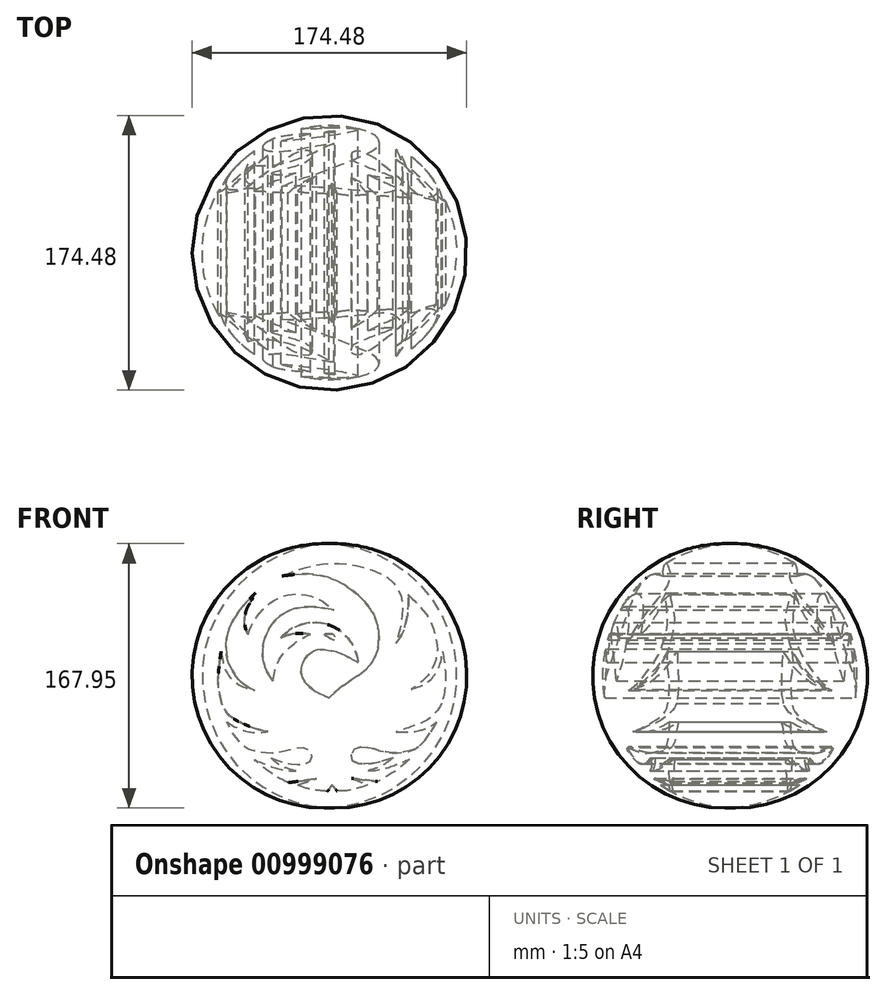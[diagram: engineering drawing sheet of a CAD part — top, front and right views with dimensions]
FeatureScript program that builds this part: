
annotation { "Feature Type Name" : "Feature", "Feature Type Description" : "" }
export const myFeature = defineFeature(function(context is Context, id is Id, definition is map)
    precondition{}
    {
        {
            var Q0;
            Q0=qCreatedBy(makeId("Front.planeOp"),FACE);
            var sketch = newSketch(context, id + "F0", { "sketchPlane" : qUnion([Q0])});
            skArc(sketch, "E0", {"start": v(18.3, 8.55) * mm, "mid": v(-1.06, 32.74) * mm, "end": v(-30.86, 24.24) * mm});
            skArc(sketch, "E1", {"start": v(-11.86, 26.45) * mm, "mid": v(-21.55, 26.98) * mm, "end": v(-30.86, 24.24) * mm});
            skFitSpline(sketch, "E2", {"points": [v(18.3, 8.55) * mm, v(12.24, 11.99) * mm, v(4.4, 15.3) * mm, v(-2.22, 16.67) * mm, v(-7.17, 16.67) * mm, v(-12.96, 14.05) * mm, v(-16.95, 8.55) * mm, v(-17.92, 2.49) * mm, v(-16.13, -3.02) * mm, v(-11.44, -7.84) * mm, v(-6.07, -11.15) * mm, v(-0.36, -13.9) * mm], "startDerivative": vector(-61.39, 36.74) * mm, "endDerivative": vector(64.34, -29.86) * mm});
            skFitSpline(sketch, "E3", {"points": [v(-11.86, 26.45) * mm, v(-18.58, 23.24) * mm, v(-27.67, 15.96) * mm, v(-32.05, 10.02) * mm, v(-34.76, 2.93) * mm, v(-35.8, -3) * mm], "startDerivative": vector(-33.06, -13.18) * mm, "endDerivative": vector(-4.26, -33.04) * mm});
            skFitSpline(sketch, "E4", {"points": [v(-35.8, -3) * mm, v(-40.57, 4.73) * mm, v(-42.38, 16.67) * mm, v(-38.38, 30.03) * mm, v(-27.54, 40.74) * mm, v(-11.86, 44.1) * mm, v(2.79, 42.03) * mm], "startDerivative": vector(-38.89, 52.02) * mm, "endDerivative": vector(81.86, -17.1) * mm});
            skFitSpline(sketch, "E5", {"points": [v(2.79, 42.03) * mm, v(-7.17, 49) * mm, v(-19.02, 52.1) * mm, v(-29.47, 50.67) * mm, v(-40.05, 44.48) * mm, v(-48.7, 33.38) * mm, v(-51.67, 26.45) * mm], "startDerivative": vector(-54.73, 44.88) * mm, "endDerivative": vector(-17.06, -47.9) * mm});
            skFitSpline(sketch, "E6", {"points": [v(-51.67, 26.45) * mm, v(-53.73, 32.48) * mm, v(-52.7, 42.03) * mm, v(-49.22, 48.6) * mm, v(-46.9, 52.87) * mm], "startDerivative": vector(-10.86, 23.04) * mm, "endDerivative": vector(10.17, 19.75) * mm});
            skFitSpline(sketch, "E7", {"points": [v(-46.9, 52.87) * mm, v(-54.25, 45.12) * mm, v(-61.86, 34.15) * mm, v(-65.22, 23.96) * mm, v(-65.22, 12.86) * mm, v(-61.86, 3.96) * mm, v(-55.67, -4.04) * mm, v(-47.6, -9.08) * mm], "startDerivative": vector(-51.07, -50.55) * mm, "endDerivative": vector(62.87, -32.4) * mm});
            skFitSpline(sketch, "E8", {"points": [v(-47.6, -9.08) * mm, v(-59.02, -4.56) * mm, v(-66.12, 4.35) * mm, v(-68.83, 15.57) * mm], "startDerivative": vector(-35.81, 9.94) * mm, "endDerivative": vector(-5.39, 34.87) * mm});
            skFitSpline(sketch, "E9", {"points": [v(-68.83, 15.57) * mm, v(-70.04, 6.24) * mm, v(-70.88, -3) * mm, v(-70.25, -9.08) * mm, v(-66.55, -21.28) * mm, v(-57.44, -28.97) * mm, v(-45.1, -33.82) * mm, v(-38.9, -35.2) * mm], "startDerivative": vector(-8.48, -64.8) * mm, "endDerivative": vector(48.51, -8.8) * mm});
            skFitSpline(sketch, "E10", {"points": [v(-38.9, -35.2) * mm, v(-42.83, -35.69) * mm, v(-51.67, -35.2) * mm, v(-61.07, -31.6) * mm, v(-65.01, -29.1) * mm], "startDerivative": vector(-18.3, -2.82) * mm, "endDerivative": vector(-16.39, 11.47) * mm});
            skFitSpline(sketch, "E11", {"points": [v(-65.01, -29.1) * mm, v(-61.9, -35.2) * mm, v(-57.73, -41.04) * mm, v(-52.83, -45.82) * mm, v(-47.6, -47.5) * mm, v(-38.9, -48.93) * mm, v(-30.13, -48.09) * mm, v(-22.6, -46.18) * mm, v(-18.42, -45.58) * mm, v(-14.36, -45.94) * mm, v(-11.86, -47.85) * mm, v(-10.9, -51.32) * mm, v(-11.86, -53.7) * mm, v(-13.76, -55.14) * mm, v(-16.89, -56.02) * mm, v(-21.98, -56.12) * mm, v(-27.17, -55.22) * mm, v(-32.46, -53.57) * mm, v(-37.1, -51.92) * mm], "startDerivative": vector(45.1, -96.86) * mm, "endDerivative": vector(-83.64, 30.1) * mm});
            skFitSpline(sketch, "E12", {"points": [v(-37.1, -51.92) * mm, v(-33.23, -55.35) * mm, v(-27.91, -58.2) * mm, v(-21.23, -60.3) * mm], "startDerivative": vector(11.85, -11.62) * mm, "endDerivative": vector(19.11, -5.3) * mm});
            skFitSpline(sketch, "E13", {"points": [v(-21.23, -60.3) * mm, v(-31, -59.24) * mm, v(-38.9, -56.71) * mm, v(-45.42, -54.09) * mm, v(-47.6, -53.05) * mm], "startDerivative": vector(-32.97, 2.11) * mm, "endDerivative": vector(-12.3, 6.16) * mm});
            skFitSpline(sketch, "E14", {"points": [v(-47.6, -53.05) * mm, v(-38.9, -60.3) * mm, v(-30.13, -65.75) * mm, v(-26.4, -67.63) * mm, v(-26.15, -67.67) * mm], "startDerivative": vector(22.9, -20.46) * mm, "endDerivative": vector(3.4, -0.2) * mm});
            skLineSegment(sketch, "E15", {"start": v(-26.15, -67.67) * mm, "end": v(-8.21, -65.2) * mm});
            skLineSegment(sketch, "E16", {"start": v(-8.21, -65.2) * mm, "end": v(-20.39, -69.18) * mm});
            skFitSpline(sketch, "E17", {"points": [v(-20.39, -69.18) * mm, v(-13.8, -71.42) * mm, v(-8.13, -72.45) * mm, v(-3.7, -72.97) * mm, v(-1.2, -73.2) * mm], "startDerivative": vector(22.05, -8.35) * mm, "endDerivative": vector(12.88, -1.05) * mm});
            skLineSegment(sketch, "E18", {"start": v(-1.2, -73.2) * mm, "end": v(1.67, -69.06) * mm});
            skLineSegment(sketch, "E19", {"start": v(1.67, -69.06) * mm, "end": v(4.86, -73) * mm});
            skLineSegment(sketch, "E20", {"start": v(1.67, -69.06) * mm, "end": v(1.67, -65.22) * mm});
            skFitSpline(sketch, "E21", {"points": [v(4.86, -73) * mm, v(12.14, -72.58) * mm, v(20, -70.6) * mm, v(24.32, -69.05) * mm], "startDerivative": vector(20.16, 0.1) * mm, "endDerivative": vector(14.12, 5.4) * mm});
            skLineSegment(sketch, "E22", {"start": v(24.32, -69.05) * mm, "end": v(13.96, -64.86) * mm});
            skLineSegment(sketch, "E23", {"start": v(13.96, -64.86) * mm, "end": v(30.45, -66.96) * mm});
            skFitSpline(sketch, "E24", {"points": [v(30.45, -66.96) * mm, v(35.72, -64.03) * mm, v(43.19, -59.36) * mm, v(50.8, -52.83) * mm], "startDerivative": vector(17.6, 9.7) * mm, "endDerivative": vector(20.16, 18.63) * mm});
            skFitSpline(sketch, "E25", {"points": [v(50.8, -52.83) * mm, v(41.87, -56.33) * mm, v(34.79, -58.74) * mm, v(29.23, -59.75) * mm, v(24.45, -60.09) * mm], "startDerivative": vector(-30.72, -12.15) * mm, "endDerivative": vector(-22.4, -1.17) * mm});
            skFitSpline(sketch, "E26", {"points": [v(24.45, -60.09) * mm, v(29.57, -58.5) * mm, v(37.53, -54.29) * mm, v(40.25, -51.79) * mm], "startDerivative": vector(14.59, 3.7) * mm, "endDerivative": vector(8.16, 8.94) * mm});
            skFitSpline(sketch, "E27", {"points": [v(40.25, -51.79) * mm, v(31.27, -54.63) * mm, v(23.31, -55.77) * mm, v(17.97, -55.31) * mm, v(15, -54.29) * mm, v(14.31, -48.51) * mm, v(18.48, -45.18) * mm, v(28.89, -46.43) * mm, v(37.53, -48.51) * mm, v(46.38, -48.37) * mm, v(55.13, -45.87) * mm, v(61.8, -39.35) * mm, v(65.13, -34.07) * mm, v(68.18, -28.94) * mm], "startDerivative": vector(-102.29, -35.69) * mm, "endDerivative": vector(44.34, 74.03) * mm});
            skFitSpline(sketch, "E28", {"points": [v(68.18, -28.94) * mm, v(63.32, -32.4) * mm, v(56.8, -34.63) * mm, v(50.8, -35.32) * mm, v(46.13, -35.35) * mm, v(42.36, -35.37) * mm], "startDerivative": vector(-21.64, -17.84) * mm, "endDerivative": vector(-22.1, -0.24) * mm});
            skFitSpline(sketch, "E29", {"points": [v(42.36, -35.37) * mm, v(47.1, -33.8) * mm, v(52.95, -31.8) * mm, v(60.34, -28.94) * mm, v(66.64, -24.16) * mm, v(69.91, -19.9) * mm, v(71.21, -17.18) * mm], "startDerivative": vector(30.04, 9.74) * mm, "endDerivative": vector(9.16, 21.69) * mm});
            skFitSpline(sketch, "E30", {"points": [v(71.21, -17.18) * mm, v(73.12, -9.28) * mm, v(73.54, 3.86) * mm, v(71.84, 15.66) * mm], "startDerivative": vector(7.57, 25.4) * mm, "endDerivative": vector(-6.06, 32.77) * mm});
            skFitSpline(sketch, "E31", {"points": [v(71.84, 15.66) * mm, v(70.15, 7.11) * mm, v(67.15, 1.22) * mm, v(61.8, -4.24) * mm, v(55.56, -7.18) * mm, v(52.02, -8.44) * mm], "startDerivative": vector(-5.78, -39.3) * mm, "endDerivative": vector(-21.64, -7.53) * mm});
            skFitSpline(sketch, "E32", {"points": [v(52.02, -8.44) * mm, v(60.2, -2.1) * mm, v(65.07, 4.39) * mm, v(68.18, 13.3) * mm, v(68.18, 21.48) * mm, v(64.52, 34.02) * mm, v(59.1, 42.41) * mm, v(50.07, 51.97) * mm], "startDerivative": vector(61.46, 43.31) * mm, "endDerivative": vector(-59.97, 60.53) * mm});
            skFitSpline(sketch, "E33", {"points": [v(50.07, 51.97) * mm, v(50.07, 43.75) * mm, v(48.15, 32.38) * mm, v(44.8, 24.37) * mm, v(42.36, 20.83) * mm], "startDerivative": vector(1.13, -30.73) * mm, "endDerivative": vector(-13.1, -17.2) * mm});
            skFitSpline(sketch, "E34", {"points": [v(42.36, 20.83) * mm, v(44.98, 30.8) * mm, v(46.2, 40.12) * mm, v(45.26, 51.97) * mm, v(37.53, 62) * mm, v(26.02, 67.69) * mm, v(10.1, 71.21) * mm, v(-10.9, 70.13) * mm, v(-30.01, 63.62) * mm], "startDerivative": vector(27.48, 94.65) * mm, "endDerivative": vector(-123.9, -50.84) * mm});
            skFitSpline(sketch, "E35", {"points": [v(-30.01, 63.62) * mm, v(-12.14, 64.75) * mm, v(6.32, 59.76) * mm, v(22.04, 47.78) * mm, v(28.65, 37.8) * mm, v(31.4, 27.82) * mm, v(29.78, 13.97) * mm, v(23.16, 4.11) * mm, v(12.9, -3.08) * mm, v(3.41, -10.32) * mm, v(-0.36, -13.9) * mm], "startDerivative": vector(152.13, 19.24) * mm, "endDerivative": vector(-51.99, -52.25) * mm});
            skFitSpline(sketch, "E36", {"points": [v(-3.1, 26.4) * mm, v(-1.48, 25.15) * mm, v(1.87, 23.43) * mm, v(3.27, 23.16) * mm, v(3.43, 24.88) * mm, v(1.81, 26.77) * mm, v(-1.42, 26.77) * mm, v(-3.1, 26.4) * mm]});
            skSolve(sketch);
        }
        {
            var Q0;
            Q0=qCreatedBy(makeId("Front.planeOp"),FACE);
            var sketch = newSketch(context, id + "F1", { "sketchPlane" : qUnion([Q0])});
            skLineSegment(sketch, "E37", {"start": v(0, 84.09) * mm, "end": v(0, -83.73) * mm});
            skArc(sketch, "E38", {"start": v(0, 84.09) * mm, "mid": v(-80.71, 0.18) * mm, "end": v(0, -83.73) * mm});
            skSolve(sketch);
        }
        {
            var Q0;
            Q0=makeQuery(id+"F1.imprint","IMPRINT",FACE,{"disambiguationData":[TD([[makeQuery(id+"F1.imprint","IMPRINT",EDGE,{"derivedFrom":sQuery(id+"F1.wireOp",EDGE,"E37")}),-1.0]])]});
            var Q1;
            Q1=sQuery(id+"F1.wireOp",EDGE,"E37");
            revolve(context, id + "F2", {"surfaceOperationType" : NewSurfaceOperationType.NEW, "entities" : qUnion([Q0]), "axis" : qUnion([Q1]), "revolveType" : RevolveType.FULL});
        }
        {
            var Q0;
            Q0 = qSketchRegion(id + "F0", true);
            extrude(context, id + "F3", {"entities" : qUnion([Q0]), "operationType" : NewBodyOperationType.REMOVE, "endBound" : BoundingType.SYMMETRIC, "depth" : 308.36 * mm, "offsetDistance" : 25.4 * mm});
        }
    });
